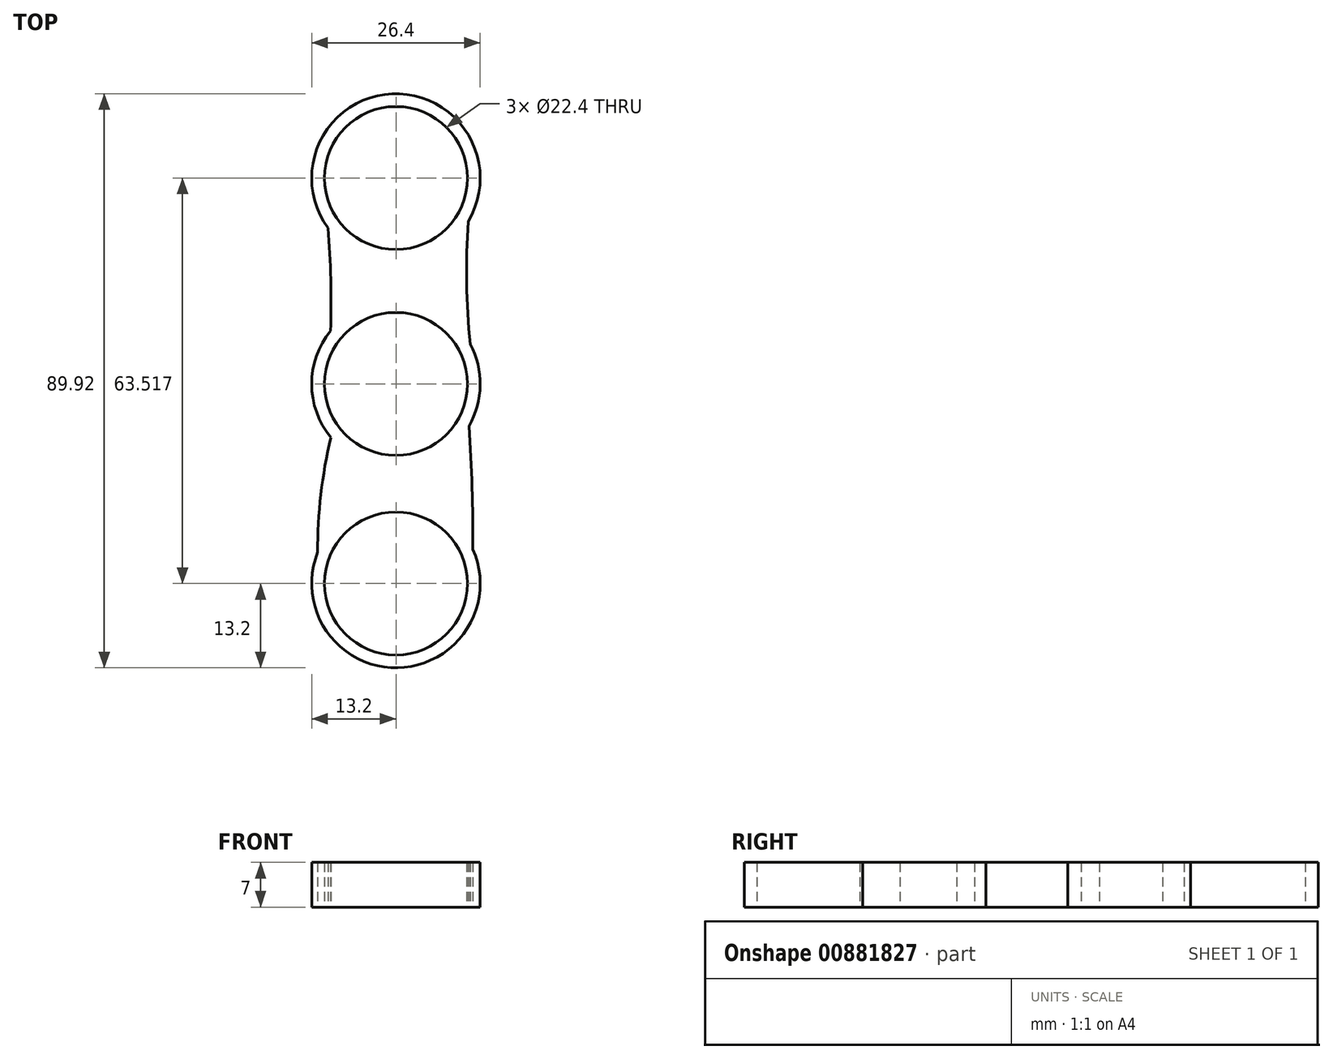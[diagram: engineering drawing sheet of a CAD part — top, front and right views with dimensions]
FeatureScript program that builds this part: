
annotation { "Feature Type Name" : "Feature", "Feature Type Description" : "" }
export const myFeature = defineFeature(function(context is Context, id is Id, definition is map)
    precondition{}
    {
        {
            var Q0;
            Q0=qCreatedBy(makeId("Top.planeOp"),FACE);
            var sketch = newSketch(context, id + "F0", { "sketchPlane" : qUnion([Q0])});
            skCircle(sketch, "E0", {"center": v(0, 0) * mm, "radius": 11.2 * mm});
            skCircle(sketch, "E1", {"center": v(0, 0) * mm, "radius": 13.2 * mm});
            skCircle(sketch, "E2", {"center": v(0, 32.26) * mm, "radius": 13.2 * mm});
            skCircle(sketch, "E3", {"center": v(0, 32.26) * mm, "radius": 11.2 * mm});
            skCircle(sketch, "E4", {"center": v(0, -31.26) * mm, "radius": 13.2 * mm});
            skCircle(sketch, "E5", {"center": v(0, -31.26) * mm, "radius": 11.2 * mm});
            skArc(sketch, "E6", {"start": v(-10.26, 8.3) * mm, "mid": v(-10.2, 16.39) * mm, "end": v(-10.64, 24.45) * mm});
            skArc(sketch, "E7", {"start": v(11.32, 25.46) * mm, "mid": v(11.08, 15.85) * mm, "end": v(11.63, 6.25) * mm});
            skArc(sketch, "E8", {"start": v(-10.2, -8.38) * mm, "mid": v(-11.76, -17.32) * mm, "end": v(-12.26, -26.38) * mm});
            skArc(sketch, "E9", {"start": v(12.06, -25.9) * mm, "mid": v(11.93, -16.24) * mm, "end": v(11.43, -6.6) * mm});
            skSolve(sketch);
        }
        {
            var Q0;
            Q0 = qSketchRegion(id + "F0", true);
            extrude(context, id + "F1", {"entities" : qUnion([Q0]), "depth" : 7 * mm, "offsetDistance" : 25 * mm});
        }
    });
